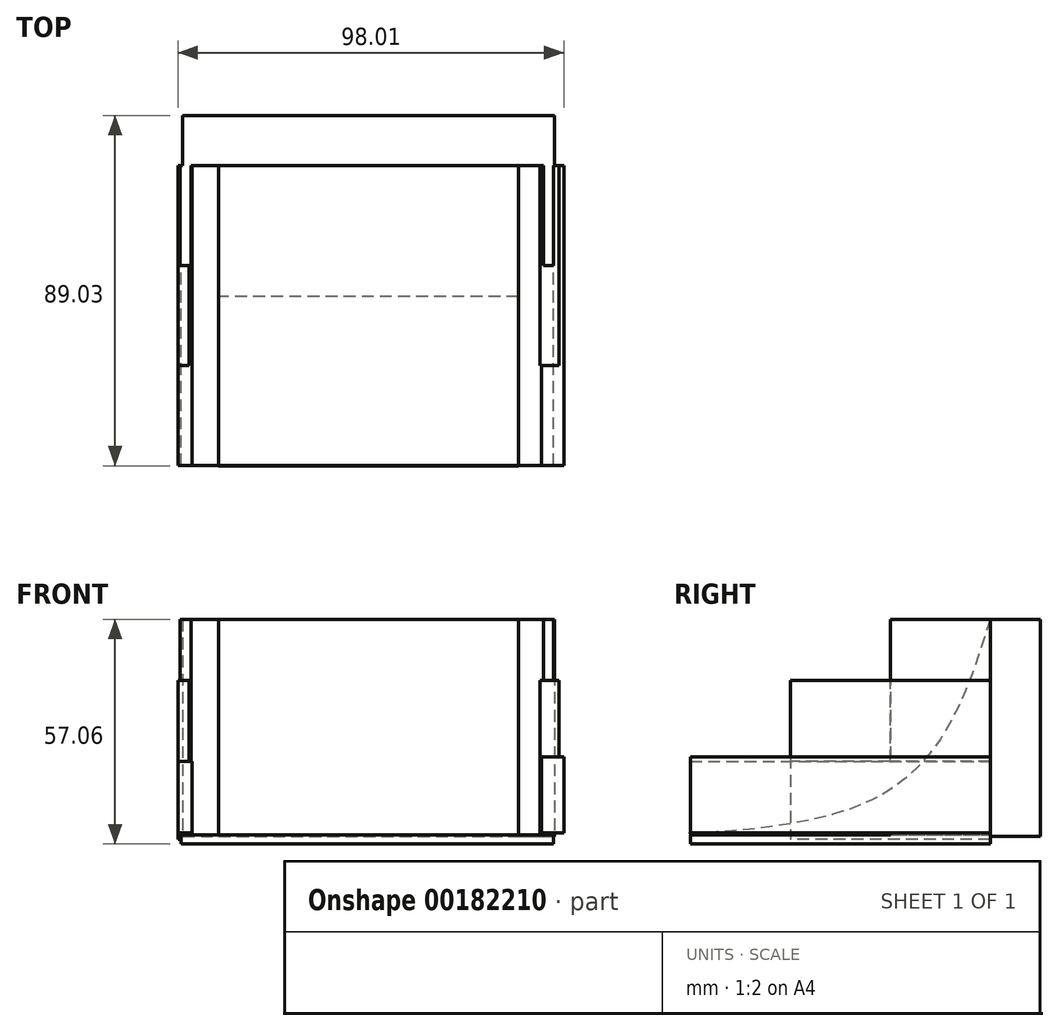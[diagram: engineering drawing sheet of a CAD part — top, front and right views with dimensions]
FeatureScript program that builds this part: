
annotation { "Feature Type Name" : "Feature", "Feature Type Description" : "" }
export const myFeature = defineFeature(function(context is Context, id is Id, definition is map)
    precondition{}
    {
        {
            var Q0;
            Q0=qCreatedBy(makeId("Top.planeOp"),FACE);
            var sketch = newSketch(context, id + "F0", { "sketchPlane" : qUnion([Q0])});
            skCircle(sketch, "E0", {"center": v(0, 0) * mm, "radius": 12.7 * mm});
            skSolve(sketch);
        }
        {
            var Q0;
            Q0=sQuery(id+"F0.wireOp",EDGE,"E0");
            extrude(context, id + "F1", {"bodyType" : ToolBodyType.SURFACE, "surfaceEntities" : qUnion([Q0]), "depth" : 609.6 * mm});
        }
        {
            var Q0;
            Q0=qCreatedBy(makeId("Front.planeOp"),FACE);
            var sketch = newSketch(context, id + "F2", { "sketchPlane" : qUnion([Q0])});
            skLineSegment(sketch, "E1.bottom", {"start": v(-47.19, 0) * mm, "end": v(47.19, 0) * mm});
            skLineSegment(sketch, "E1.top", {"start": v(-47.19, -55.06) * mm, "end": v(47.19, -55.06) * mm});
            skLineSegment(sketch, "E1.left", {"start": v(-47.19, 0) * mm, "end": v(-47.19, -55.06) * mm});
            skLineSegment(sketch, "E1.right", {"start": v(47.19, 0) * mm, "end": v(47.19, -55.06) * mm});
            skSolve(sketch);
        }
        {
            var Q0;
            Q0=makeQuery(id+"F2.imprint","IMPRINT",FACE,{"disambiguationData":[TD([[makeQuery(id+"F2.imprint","IMPRINT",EDGE,{"derivedFrom":sQuery(id+"F2.wireOp",EDGE,"E1.bottom")}),-1.0]])]});
            extrude(context, id + "F3", {"entities" : qUnion([Q0]), "oppositeDirection" : true, "depth" : 12.7 * mm});
        }
        {
            var Q0;
            Q0=qCreatedBy(makeId("Front.planeOp"),FACE);
            var sketch = newSketch(context, id + "F4", { "sketchPlane" : qUnion([Q0])});
            skLineSegment(sketch, "E2.bottom", {"start": v(-47.6, -54.8) * mm, "end": v(46.97, -54.8) * mm});
            skLineSegment(sketch, "E2.top", {"start": v(-47.6, -57.06) * mm, "end": v(46.97, -57.06) * mm});
            skLineSegment(sketch, "E2.left", {"start": v(-47.6, -54.8) * mm, "end": v(-47.6, -57.06) * mm});
            skLineSegment(sketch, "E2.right", {"start": v(46.97, -54.8) * mm, "end": v(46.97, -57.06) * mm});
            skSolve(sketch);
        }
        {
            var Q0;
            Q0=makeQuery(id+"F4.imprint","IMPRINT",FACE,{"disambiguationData":[TD([[makeQuery(id+"F4.imprint","IMPRINT",EDGE,{"derivedFrom":sQuery(id+"F4.wireOp",EDGE,"E2.bottom")}),-1.0]])]});
            extrude(context, id + "F5", {"entities" : qUnion([Q0]), "operationType" : NewBodyOperationType.ADD, "depth" : 76.2 * mm});
        }
        {
            var Q0;
            Q0=qCreatedBy(makeId("Front.planeOp"),FACE);
            var sketch = newSketch(context, id + "F6", { "sketchPlane" : qUnion([Q0])});
            skLineSegment(sketch, "E3.bottom", {"start": v(-47.89, 0) * mm, "end": v(-45.05, 0) * mm});
            skLineSegment(sketch, "E3.top", {"start": v(-47.89, -54.93) * mm, "end": v(-45.05, -54.93) * mm});
            skLineSegment(sketch, "E3.left", {"start": v(-47.89, 0) * mm, "end": v(-47.89, -54.93) * mm});
            skLineSegment(sketch, "E3.right", {"start": v(-45.05, 0) * mm, "end": v(-45.05, -54.93) * mm});
            skLineSegment(sketch, "E4.MirrorCS", {"start": v(47.89, 0) * mm, "end": v(47.89, -54.93) * mm});
            skLineSegment(sketch, "E5.MirrorCS", {"start": v(45.05, 0) * mm, "end": v(45.05, -54.93) * mm});
            skLineSegment(sketch, "E6.MirrorCS", {"start": v(47.89, 0) * mm, "end": v(45.05, 0) * mm});
            skLineSegment(sketch, "E7.MirrorCS", {"start": v(47.89, -54.93) * mm, "end": v(45.05, -54.93) * mm});
            skSolve(sketch);
        }
        {
            var Q0;
            Q0=makeQuery(id+"F6.imprint","IMPRINT",FACE,{"disambiguationData":[TD([[makeQuery(id+"F6.imprint","IMPRINT",EDGE,{"derivedFrom":sQuery(id+"F6.wireOp",EDGE,"E3.bottom")}),-1.0]])]});
            extrude(context, id + "F7", {"entities" : qUnion([Q0]), "operationType" : NewBodyOperationType.ADD, "depth" : 25.4 * mm});
        }
        {
            var Q0;
            Q0=qCreatedBy(makeId("Front.planeOp"),FACE);
            var sketch = newSketch(context, id + "F8", { "sketchPlane" : qUnion([Q0])});
            skLineSegment(sketch, "E8.bottom", {"start": v(44.4, 0) * mm, "end": v(46.98, 0) * mm});
            skLineSegment(sketch, "E8.top", {"start": v(44.4, -54.85) * mm, "end": v(46.98, -54.85) * mm});
            skLineSegment(sketch, "E8.left", {"start": v(44.4, 0) * mm, "end": v(44.4, -54.85) * mm});
            skLineSegment(sketch, "E8.right", {"start": v(46.98, 0) * mm, "end": v(46.98, -54.85) * mm});
            skSolve(sketch);
        }
        {
            var Q0;
            Q0=makeQuery(id+"F8.imprint","IMPRINT",FACE,{"disambiguationData":[TD([[makeQuery(id+"F8.imprint","IMPRINT",EDGE,{"derivedFrom":sQuery(id+"F8.wireOp",EDGE,"E8.bottom")}),-1.0]])]});
            extrude(context, id + "F9", {"entities" : qUnion([Q0]), "operationType" : NewBodyOperationType.ADD, "depth" : 25.4 * mm});
        }
        {
            var Q0;
            Q0=qCreatedBy(makeId("Front.planeOp"),FACE);
            var sketch = newSketch(context, id + "F10", { "sketchPlane" : qUnion([Q0])});
            skLineSegment(sketch, "E9.bottom", {"start": v(-48.4, -15.54) * mm, "end": v(-45.58, -15.54) * mm});
            skLineSegment(sketch, "E9.top", {"start": v(-48.4, -55.87) * mm, "end": v(-45.58, -55.87) * mm});
            skLineSegment(sketch, "E9.left", {"start": v(-48.4, -15.54) * mm, "end": v(-48.4, -55.87) * mm});
            skLineSegment(sketch, "E9.right", {"start": v(-45.58, -15.54) * mm, "end": v(-45.58, -55.87) * mm});
            skSolve(sketch);
        }
        {
            var Q0;
            Q0=makeQuery(id+"F10.imprint","IMPRINT",FACE,{"disambiguationData":[TD([[makeQuery(id+"F10.imprint","IMPRINT",EDGE,{"derivedFrom":sQuery(id+"F10.wireOp",EDGE,"E9.bottom")}),-1.0]])]});
            extrude(context, id + "F11", {"entities" : qUnion([Q0]), "operationType" : NewBodyOperationType.ADD, "depth" : 50.8 * mm});
        }
        {
            var Q0;
            Q0=qCreatedBy(makeId("Front.planeOp"),FACE);
            var sketch = newSketch(context, id + "F12", { "sketchPlane" : qUnion([Q0])});
            skLineSegment(sketch, "E10.bottom", {"start": v(43.56, -54.26) * mm, "end": v(48.4, -54.26) * mm});
            skLineSegment(sketch, "E10.top", {"start": v(43.56, -15.54) * mm, "end": v(48.4, -15.54) * mm});
            skLineSegment(sketch, "E10.left", {"start": v(43.56, -54.26) * mm, "end": v(43.56, -15.54) * mm});
            skLineSegment(sketch, "E10.right", {"start": v(48.4, -54.26) * mm, "end": v(48.4, -15.54) * mm});
            skSolve(sketch);
        }
        {
            var Q0;
            Q0=makeQuery(id+"F12.imprint","IMPRINT",FACE,{"disambiguationData":[TD([[makeQuery(id+"F12.imprint","IMPRINT",EDGE,{"derivedFrom":sQuery(id+"F12.wireOp",EDGE,"E10.bottom")}),1.0]])]});
            extrude(context, id + "F13", {"entities" : qUnion([Q0]), "operationType" : NewBodyOperationType.ADD, "depth" : 50.8 * mm});
        }
        {
            var Q0;
            Q0=qCreatedBy(makeId("Right.planeOp"),FACE);
            var sketch = newSketch(context, id + "F14", { "sketchPlane" : qUnion([Q0])});
            skFitSpline(sketch, "E11", {"points": [v(0, 0) * mm, v(-29.85, -45.79) * mm, v(-76.23, -54.26) * mm, v(0, -55.07) * mm], "startDerivative": vector(-54.26, -172.02) * mm, "endDerivative": vector(310.4, -2.48) * mm});
            skLineSegment(sketch, "E12", {"start": v(0, 0) * mm, "end": v(0, -55.07) * mm});
            skSolve(sketch);
        }
        {
            var Q0;
            Q0=makeQuery(id+"F14.imprint","IMPRINT",FACE,{"disambiguationData":[TD([[makeQuery(id+"F14.imprint","IMPRINT",EDGE,{"derivedFrom":sQuery(id+"F14.wireOp",EDGE,"E11")}),1.0]])]});
            extrude(context, id + "F15", {"entities" : qUnion([Q0]), "operationType" : NewBodyOperationType.ADD, "depth" : 38.1 * mm, "hasSecondDirection" : true, "secondDirectionOppositeDirection" : true, "secondDirectionDepth" : 38.1 * mm});
        }
        {
            var Q0;
            Q0=qCreatedBy(makeId("Front.planeOp"),FACE);
            var sketch = newSketch(context, id + "F16", { "sketchPlane" : qUnion([Q0])});
            skLineSegment(sketch, "E13.bottom", {"start": v(-48.4, -36.1) * mm, "end": v(-44.77, -36.1) * mm});
            skLineSegment(sketch, "E13.top", {"start": v(-48.4, -54.26) * mm, "end": v(-44.77, -54.26) * mm});
            skLineSegment(sketch, "E13.left", {"start": v(-48.4, -36.1) * mm, "end": v(-48.4, -54.26) * mm});
            skLineSegment(sketch, "E13.right", {"start": v(-44.77, -36.1) * mm, "end": v(-44.77, -54.26) * mm});
            skSolve(sketch);
        }
        {
            var Q0;
            Q0=makeQuery(id+"F16.imprint","IMPRINT",FACE,{"disambiguationData":[TD([[makeQuery(id+"F16.imprint","IMPRINT",EDGE,{"derivedFrom":sQuery(id+"F16.wireOp",EDGE,"E13.bottom")}),-1.0]])]});
            extrude(context, id + "F17", {"entities" : qUnion([Q0]), "operationType" : NewBodyOperationType.ADD, "depth" : 76.2 * mm});
        }
        {
            var Q0;
            Q0=qCreatedBy(makeId("Front.planeOp"),FACE);
            var sketch = newSketch(context, id + "F18", { "sketchPlane" : qUnion([Q0])});
            skLineSegment(sketch, "E14.bottom", {"start": v(43.96, -54.26) * mm, "end": v(49.6, -54.26) * mm});
            skLineSegment(sketch, "E14.top", {"start": v(43.96, -34.9) * mm, "end": v(49.6, -34.9) * mm});
            skLineSegment(sketch, "E14.left", {"start": v(43.96, -54.26) * mm, "end": v(43.96, -34.9) * mm});
            skLineSegment(sketch, "E14.right", {"start": v(49.6, -54.26) * mm, "end": v(49.6, -34.9) * mm});
            skSolve(sketch);
        }
        {
            var Q0;
            Q0=makeQuery(id+"F18.imprint","IMPRINT",FACE,{"disambiguationData":[TD([[makeQuery(id+"F18.imprint","IMPRINT",EDGE,{"derivedFrom":sQuery(id+"F18.wireOp",EDGE,"E14.bottom")}),1.0]])]});
            extrude(context, id + "F19", {"entities" : qUnion([Q0]), "operationType" : NewBodyOperationType.ADD, "depth" : 76.2 * mm});
        }
    });
